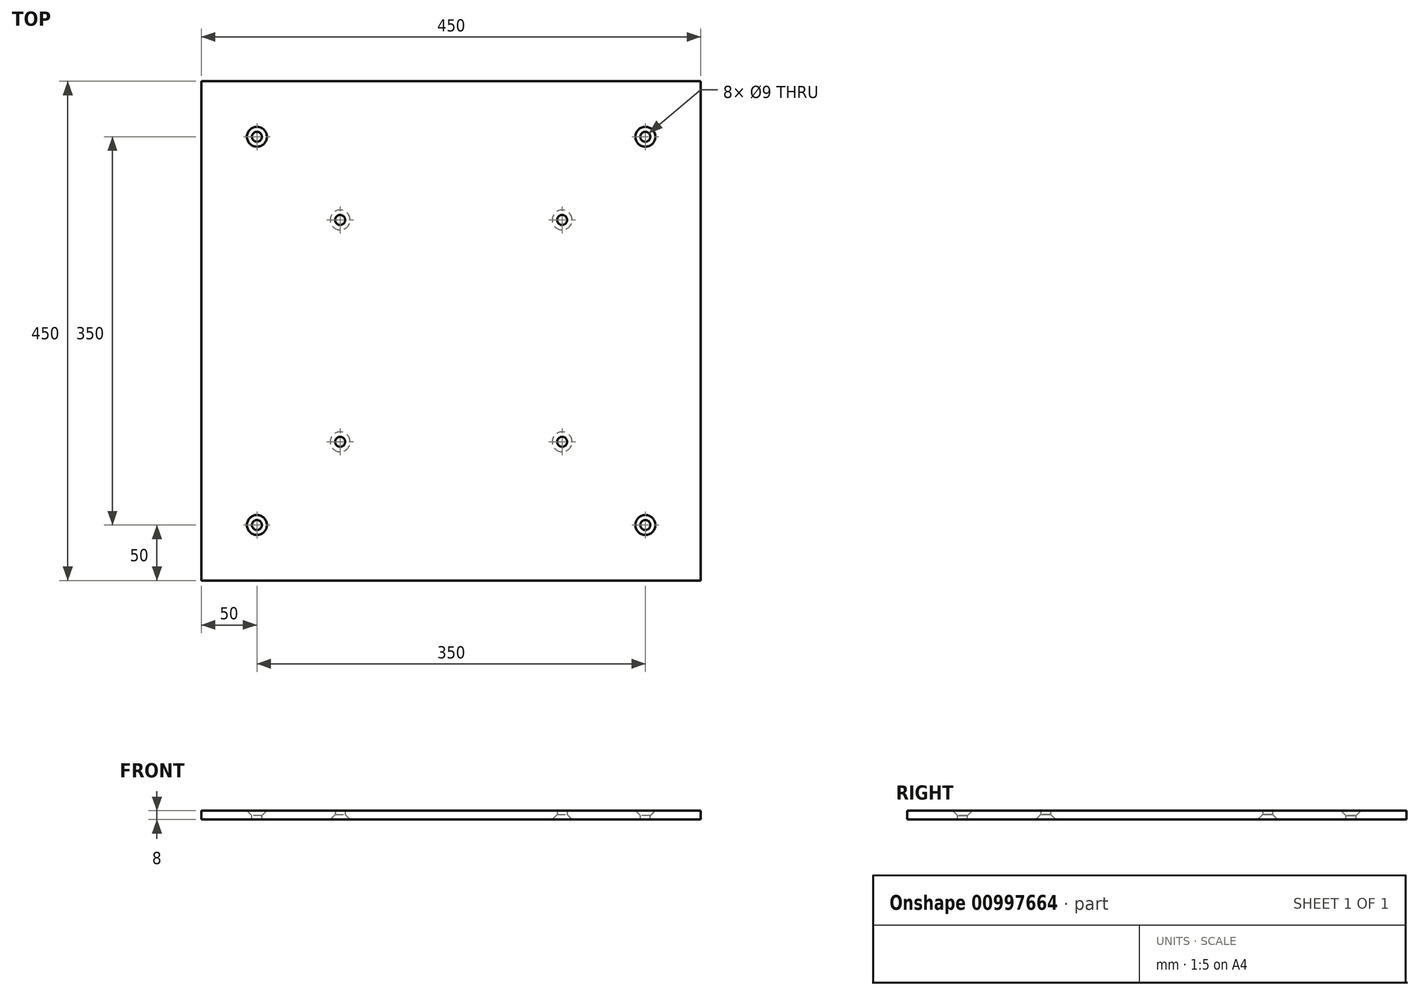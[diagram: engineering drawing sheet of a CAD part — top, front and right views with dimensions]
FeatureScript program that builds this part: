
annotation { "Feature Type Name" : "Feature", "Feature Type Description" : "" }
export const myFeature = defineFeature(function(context is Context, id is Id, definition is map)
    precondition{}
    {
        {
            var Q0;
            Q0=qCreatedBy(makeId("Top.planeOp"),FACE);
            var sketch = newSketch(context, id + "F0", { "sketchPlane" : qUnion([Q0])});
            skLineSegment(sketch, "E0.bottom", {"start": v(0, 0) * mm, "end": v(450, 0) * mm});
            skLineSegment(sketch, "E0.top", {"start": v(0, -450) * mm, "end": v(450, -450) * mm});
            skLineSegment(sketch, "E0.left", {"start": v(0, 0) * mm, "end": v(0, -450) * mm});
            skLineSegment(sketch, "E0.right", {"start": v(450, 0) * mm, "end": v(450, -450) * mm});
            skSolve(sketch);
        }
        {
            var Q0;
            Q0=makeQuery(id+"F0.imprint","IMPRINT",FACE,{"disambiguationData":[TD([[makeQuery(id+"F0.imprint","IMPRINT",EDGE,{"derivedFrom":sQuery(id+"F0.wireOp",EDGE,"E0.bottom")}),-1.0]])]});
            extrude(context, id + "F1", {"entities" : qUnion([Q0]), "depth" : 8 * mm, "offsetDistance" : 25 * mm});
        }
        {
            var Q0;
            Q0=makeQuery(id+"F1.opExtrude","CAP_FACE",FACE,{"disambiguationData":[OSD([sQuery(id+"F0.wireOp",EDGE,"E0.bottom"),sQuery(id+"F0.wireOp",EDGE,"E0.top"),sQuery(id+"F0.wireOp",EDGE,"E0.left"),sQuery(id+"F0.wireOp",EDGE,"E0.right")])],"isStart":false});
            var sketch = newSketch(context, id + "F2", { "sketchPlane" : qUnion([Q0])});
            skPoint(sketch, "E1", {"position": v(50, -400) * mm});
            skPoint(sketch, "E2.0.1.0", {"position": v(50, -50) * mm});
            skPoint(sketch, "E2.1.0.0", {"position": v(400, -400) * mm});
            skPoint(sketch, "E2.1.1.0", {"position": v(400, -50) * mm});
            skLineSegment(sketch, "E2.direction1", {"start": v(50, -400) * mm, "end": v(400, -400) * mm, "construction": true});
            skLineSegment(sketch, "E2.direction2", {"start": v(50, -400) * mm, "end": v(50, -50) * mm, "construction": true});
            skSolve(sketch);
        }
        {
            var Q0;
            Q0=sQuery(id+"F2.wireOp",VERTEX,"E1");
            var Q1;
            Q1=sQuery(id+"F2.wireOp",VERTEX,"E2.1.0.0");
            var Q2;
            Q2=sQuery(id+"F2.wireOp",VERTEX,"E2.1.1.0");
            var Q3;
            Q3=sQuery(id+"F2.wireOp",VERTEX,"E2.0.1.0");
            var Q4;
            Q4=makeQuery(id+"F1.opExtrude","SWEPT_BODY",BODY,{"disambiguationData":[OSD([sQuery(id+"F0.wireOp",EDGE,"E0.bottom"),sQuery(id+"F0.wireOp",EDGE,"E0.top"),sQuery(id+"F0.wireOp",EDGE,"E0.left"),sQuery(id+"F0.wireOp",EDGE,"E0.right")])]});
            hole(context, id + "F3", {"style" : HoleStyle.C_SINK, "endStyle" : HoleEndStyle.THROUGH, "standardTappedOrClearance" : lookupTablePath({ "fit" : "Normal", "standard" : "ISO", "size" : "M8", "type" : "Clearance" }), "standardBlindInLast" : lookupTablePath({ "fit" : "Normal", "standard" : "ISO", "engagement" : "75%", "pitch" : "1.25 mm", "size" : "M8", "type" : "Clearance & tapped" }), "holeDiameter" : 9 * mm, "cSinkDiameter" : 17.92 * mm, "cSinkAngle" : 90 * degree, "majorDiameter" : 5 * mm, "isTappedThrough" : true, "tappedDepth" : 12 * mm, "tapClearance" : 3, "locations" : qUnion([Q0, Q1, Q2, Q3]), "scope" : qUnion([Q4])});
        }
        {
            var Q0;
            Q0=makeQuery(id+"F1.opExtrude","CAP_FACE",FACE,{"disambiguationData":[OSD([sQuery(id+"F0.wireOp",EDGE,"E0.bottom"),sQuery(id+"F0.wireOp",EDGE,"E0.top"),sQuery(id+"F0.wireOp",EDGE,"E0.left"),sQuery(id+"F0.wireOp",EDGE,"E0.right")])],"isStart":true});
            var sketch = newSketch(context, id + "F4", { "sketchPlane" : qUnion([Q0])});
            skLineSegment(sketch, "E3.bottom", {"start": v(125, 325) * mm, "end": v(325, 325) * mm, "construction": true});
            skLineSegment(sketch, "E3.top", {"start": v(125, 125) * mm, "end": v(325, 125) * mm, "construction": true});
            skLineSegment(sketch, "E3.left", {"start": v(125, 325) * mm, "end": v(125, 125) * mm, "construction": true});
            skLineSegment(sketch, "E3.right", {"start": v(325, 325) * mm, "end": v(325, 125) * mm, "construction": true});
            skSolve(sketch);
        }
        {
            var Q0;
            Q0=sQuery(id+"F4.wireOp",VERTEX,"E3.bottom.start");
            var Q1;
            Q1=sQuery(id+"F4.wireOp",VERTEX,"E3.top.end");
            var Q2;
            Q2=sQuery(id+"F4.wireOp",VERTEX,"E3.bottom.end");
            var Q3;
            Q3=sQuery(id+"F4.wireOp",VERTEX,"E3.top.start");
            var Q4;
            Q4=makeQuery(id+"F1.opExtrude","SWEPT_BODY",BODY,{"disambiguationData":[OSD([sQuery(id+"F0.wireOp",EDGE,"E0.bottom"),sQuery(id+"F0.wireOp",EDGE,"E0.top"),sQuery(id+"F0.wireOp",EDGE,"E0.left"),sQuery(id+"F0.wireOp",EDGE,"E0.right")])]});
            hole(context, id + "F5", {"style" : HoleStyle.C_SINK, "endStyle" : HoleEndStyle.THROUGH, "standardTappedOrClearance" : lookupTablePath({ "fit" : "Normal", "standard" : "ISO", "size" : "M8", "type" : "Clearance" }), "standardBlindInLast" : lookupTablePath({ "fit" : "Normal", "standard" : "ISO", "engagement" : "75%", "pitch" : "1.25 mm", "size" : "M8", "type" : "Clearance & tapped" }), "holeDiameter" : 9 * mm, "cSinkDiameter" : 17.92 * mm, "cSinkAngle" : 90 * degree, "majorDiameter" : 5 * mm, "isTappedThrough" : true, "tappedDepth" : 12 * mm, "tapClearance" : 3, "locations" : qUnion([Q0, Q1, Q2, Q3]), "scope" : qUnion([Q4])});
        }
    });
